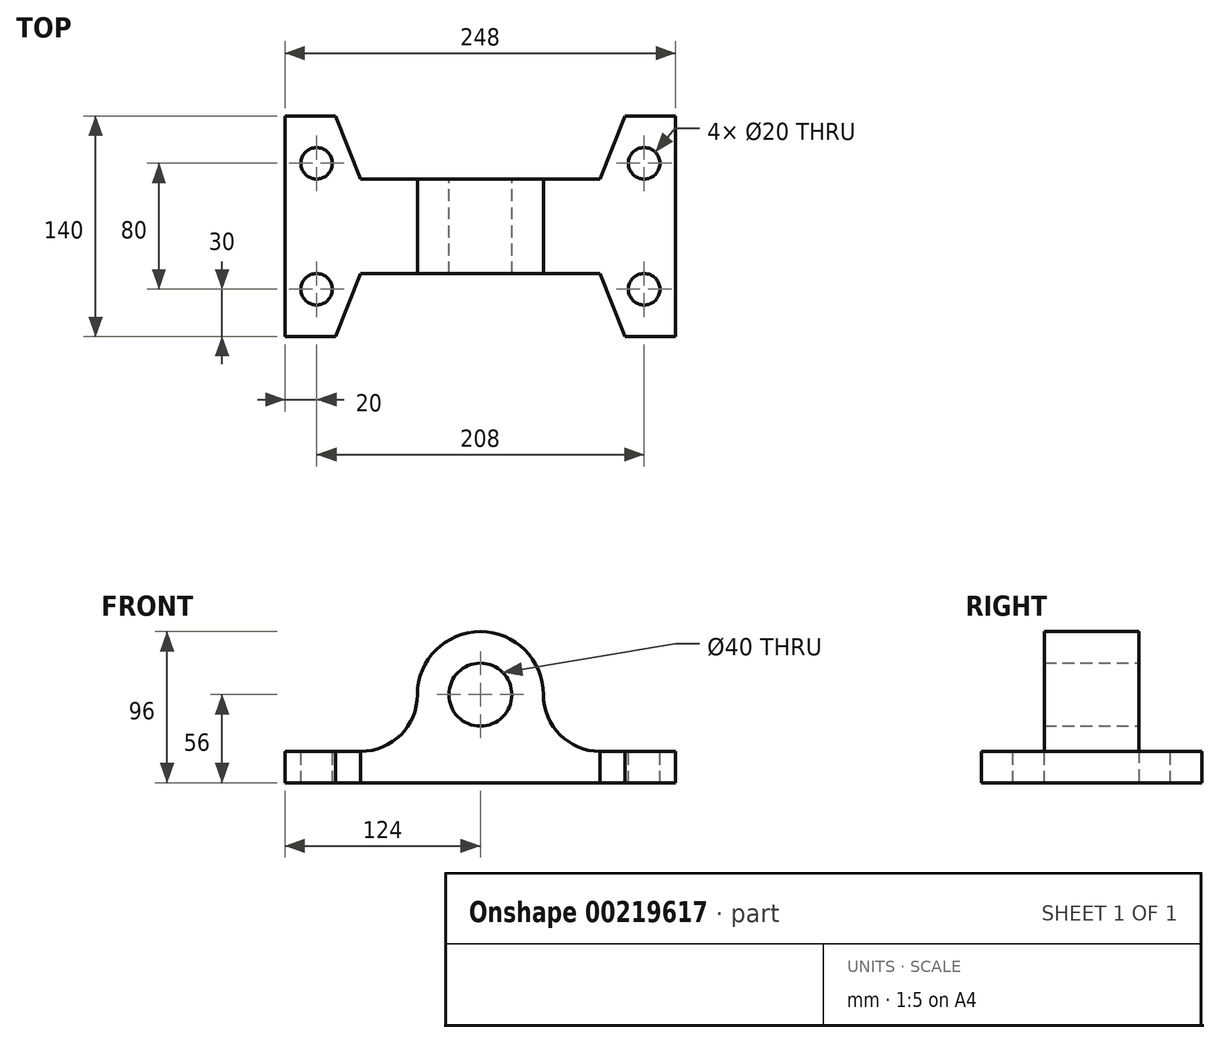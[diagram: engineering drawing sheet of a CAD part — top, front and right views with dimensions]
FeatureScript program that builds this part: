
annotation { "Feature Type Name" : "Feature", "Feature Type Description" : "" }
export const myFeature = defineFeature(function(context is Context, id is Id, definition is map)
    precondition{}
    {
        {
            var Q0;
            Q0=qCreatedBy(makeId("Front.planeOp"),FACE);
            var sketch = newSketch(context, id + "F0", { "sketchPlane" : qUnion([Q0])});
            skCircle(sketch, "E0", {"center": v(0, 0) * mm, "radius": 20 * mm});
            skArc(sketch, "E1", {"start": v(40, 0) * mm, "mid": v(0, 40) * mm, "end": v(-40, 0) * mm});
            skArc(sketch, "E2", {"start": v(-40, 0) * mm, "mid": v(-50.54, -25.46) * mm, "end": v(-76, -36) * mm});
            skArc(sketch, "E3", {"start": v(40, 0) * mm, "mid": v(50.54, -25.46) * mm, "end": v(76, -36) * mm});
            skLineSegment(sketch, "E4", {"start": v(76, -36) * mm, "end": v(76, -56) * mm});
            skLineSegment(sketch, "E5", {"start": v(76, -56) * mm, "end": v(-76, -56) * mm});
            skLineSegment(sketch, "E6", {"start": v(-76, -56) * mm, "end": v(-76, -36) * mm});
            skSolve(sketch);
        }
        {
            var Q0;
            Q0=makeQuery(id+"F0.imprint","IMPRINT",FACE,{"disambiguationData":[TD([[makeQuery(id+"F0.imprint","IMPRINT",EDGE,{"derivedFrom":sQuery(id+"F0.wireOp",EDGE,"E0")}),-1.0]])]});
            extrude(context, id + "F1", {"entities" : qUnion([Q0]), "depth" : 60 * mm});
        }
        {
            var Q0;
            Q0=makeQuery(id+"F1.opExtrude","SWEPT_FACE",FACE,{"disambiguationData":[OSD([sQuery(id+"F0.wireOp",EDGE,"E4")])]});
            var sketch = newSketch(context, id + "F2", { "sketchPlane" : qUnion([Q0])});
            skLineSegment(sketch, "E7", {"start": v(-60, -36) * mm, "end": v(-100, -36) * mm});
            skLineSegment(sketch, "E8", {"start": v(-100, -36) * mm, "end": v(-100, -56) * mm});
            skLineSegment(sketch, "E9", {"start": v(-100, -56) * mm, "end": v(40, -56) * mm});
            skLineSegment(sketch, "E10", {"start": v(40, -56) * mm, "end": v(40, -36) * mm});
            skLineSegment(sketch, "E11", {"start": v(40, -36) * mm, "end": v(0, -36) * mm});
            skLineSegment(sketch, "E12", {"start": v(0, -36) * mm, "end": v(-60, -36) * mm});
            skSolve(sketch);
        }
        {
            var Q0;
            Q0=makeQuery(id+"F2.imprint","IMPRINT",FACE,{"disambiguationData":[TD([[makeQuery(id+"F2.imprint","IMPRINT",EDGE,{"derivedFrom":sQuery(id+"F2.wireOp",EDGE,"E7")}),1.0]])]});
            var Q1;
            {var subQ2=sQuery(id+"F2.wireOp",EDGE,"E10");Q1=makeQuery(id+"F2.imprint","IMPRINT",FACE,{"disambiguationData":[TD([[makeQuery(id+"F2.imprint","IMPRINT",EDGE,{"derivedFrom":subQ2}),1.0]])]});}
            var Q2;
            Q2=makeQuery(id+"F2.imprint","IMPRINT",FACE,{"disambiguationData":[TD([[makeQuery(id+"F2.imprint","IMPRINT",EDGE,{"derivedFrom":sQuery(id+"F2.wireOp",EDGE,"E12")}),-1.0]])]});
            extrude(context, id + "F3", {"entities" : qUnion([Q0, Q1, Q2]), "operationType" : NewBodyOperationType.ADD, "depth" : 48 * mm});
        }
        {
            var Q0;
            Q0=makeQuery(id+"F3.opExtrude","SWEPT_FACE",FACE,{"disambiguationData":[OSD([sQuery(id+"F2.wireOp",EDGE,"E7"),sQuery(id+"F2.wireOp",EDGE,"E11"),sQuery(id+"F2.wireOp",EDGE,"E12")])]});
            var sketch = newSketch(context, id + "F4", { "sketchPlane" : qUnion([Q0])});
            skLineSegment(sketch, "E13", {"start": v(92, 40) * mm, "end": v(76, 0) * mm});
            skLineSegment(sketch, "E14", {"start": v(76, 0) * mm, "end": v(76, 40) * mm});
            skLineSegment(sketch, "E15", {"start": v(76, 40) * mm, "end": v(92, 40) * mm});
            skLineSegment(sketch, "E16", {"start": v(92, -100) * mm, "end": v(76, -60) * mm});
            skLineSegment(sketch, "E17", {"start": v(76, -60) * mm, "end": v(76, -100) * mm});
            skLineSegment(sketch, "E18", {"start": v(76, -100) * mm, "end": v(92, -100) * mm});
            skSolve(sketch);
        }
        {
            var Q0;
            Q0 = qSketchRegion(id + "F4", true);
            extrude(context, id + "F5", {"entities" : qUnion([Q0]), "operationType" : NewBodyOperationType.REMOVE, "endBound" : BoundingType.THROUGH_ALL, "oppositeDirection" : true, "depth" : 25 * mm});
        }
        {
            var Q0;
            Q0=makeQuery(id+"F1.opExtrude","SWEPT_BODY",BODY,{"disambiguationData":[OSD([sQuery(id+"F0.wireOp",EDGE,"E0"),sQuery(id+"F0.wireOp",EDGE,"E1"),sQuery(id+"F0.wireOp",EDGE,"E2"),sQuery(id+"F0.wireOp",EDGE,"E3"),sQuery(id+"F0.wireOp",EDGE,"E4"),sQuery(id+"F0.wireOp",EDGE,"E5"),sQuery(id+"F0.wireOp",EDGE,"E6")])]});
            var Q1;
            Q1=qCreatedBy(makeId("Right.planeOp"),FACE);
            mirror(context, id + "F6", {"operationType" : NewBodyOperationType.ADD, "entities" : qUnion([Q0]), "mirrorPlane" : qUnion([Q1])});
        }
        {
            var Q0;
            Q0=makeQuery(id+"F6.opPattern","COPY",FACE,{"derivedFrom":makeQuery(id+"F3.opExtrude","SWEPT_FACE",FACE,{"disambiguationData":[OSD([sQuery(id+"F2.wireOp",EDGE,"E7"),sQuery(id+"F2.wireOp",EDGE,"E11"),sQuery(id+"F2.wireOp",EDGE,"E12")])]}),"instanceName":"1"});
            var sketch = newSketch(context, id + "F7", { "sketchPlane" : qUnion([Q0])});
            skCircle(sketch, "E19", {"center": v(-104, 10) * mm, "radius": 10 * mm});
            skCircle(sketch, "E20", {"center": v(-104, -70) * mm, "radius": 10 * mm});
            skSolve(sketch);
        }
        {
            var Q0;
            Q0=makeQuery(id+"F7.imprint","IMPRINT",FACE,{"disambiguationData":[TD([[makeQuery(id+"F7.imprint","IMPRINT",EDGE,{"derivedFrom":sQuery(id+"F7.wireOp",EDGE,"E20")}),1.0]])]});
            var Q1;
            Q1=makeQuery(id+"F7.imprint","IMPRINT",FACE,{"disambiguationData":[TD([[makeQuery(id+"F7.imprint","IMPRINT",EDGE,{"derivedFrom":sQuery(id+"F7.wireOp",EDGE,"E19")}),1.0]])]});
            extrude(context, id + "F8", {"entities" : qUnion([Q0, Q1]), "operationType" : NewBodyOperationType.REMOVE, "endBound" : BoundingType.THROUGH_ALL, "oppositeDirection" : true, "depth" : 25 * mm});
        }
        {
            var Q0;
            Q0=makeQuery(id+"F1.opExtrude","SWEPT_BODY",BODY,{"disambiguationData":[OSD([sQuery(id+"F0.wireOp",EDGE,"E0"),sQuery(id+"F0.wireOp",EDGE,"E1"),sQuery(id+"F0.wireOp",EDGE,"E2"),sQuery(id+"F0.wireOp",EDGE,"E3"),sQuery(id+"F0.wireOp",EDGE,"E4"),sQuery(id+"F0.wireOp",EDGE,"E5"),sQuery(id+"F0.wireOp",EDGE,"E6")])]});
            var Q1;
            Q1=qCreatedBy(makeId("Right.planeOp"),FACE);
            mirror(context, id + "F9", {"operationType" : NewBodyOperationType.INTERSECT, "entities" : qUnion([Q0]), "mirrorPlane" : qUnion([Q1])});
        }
    });
